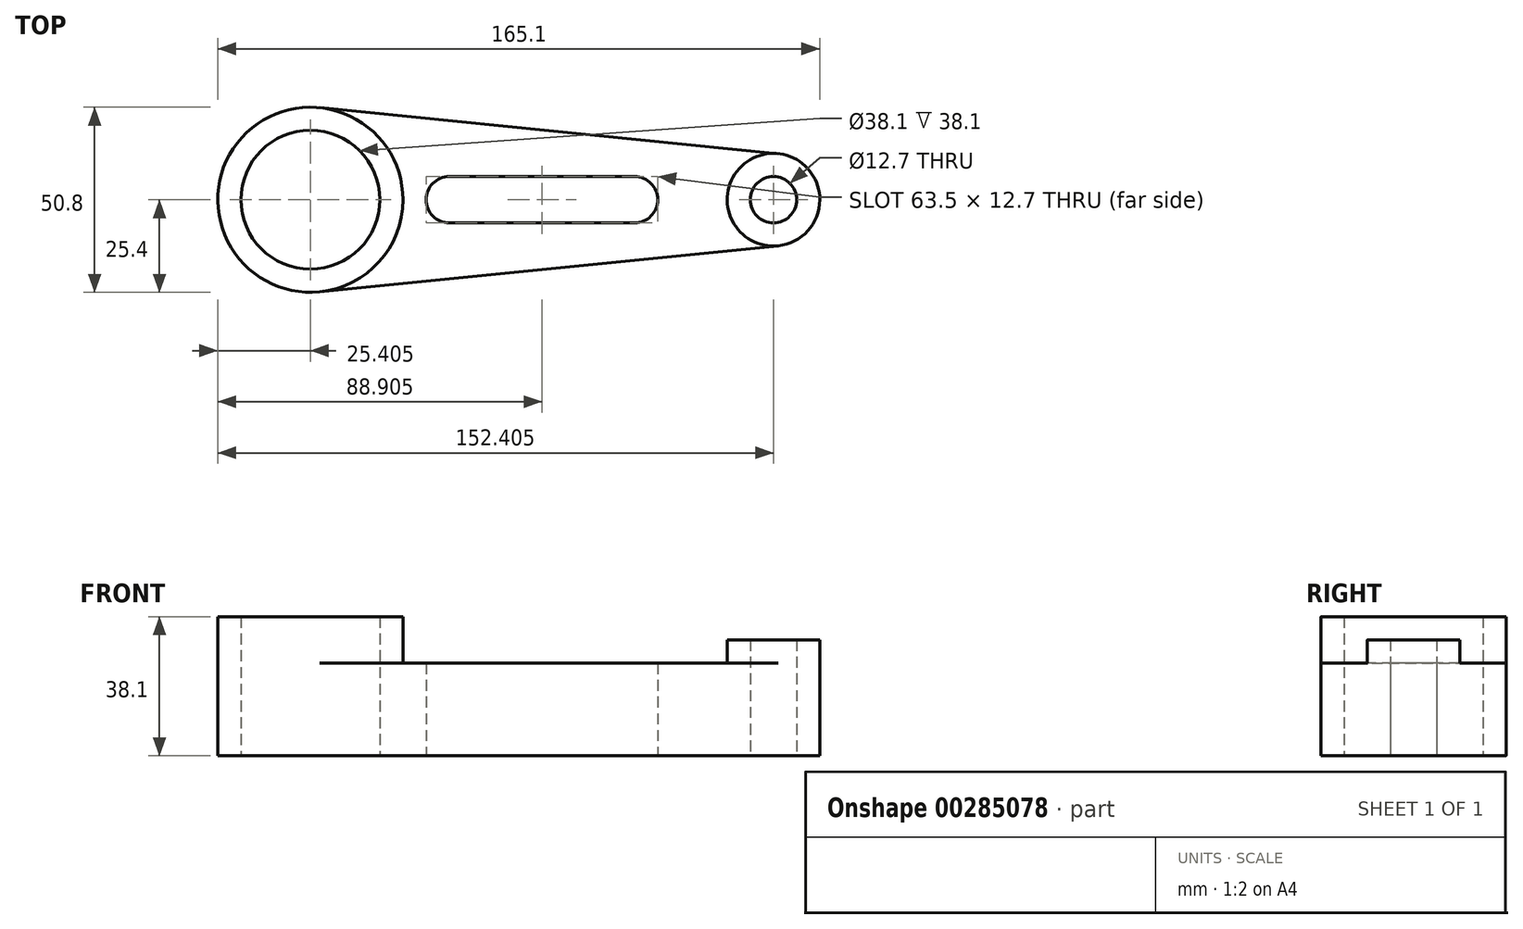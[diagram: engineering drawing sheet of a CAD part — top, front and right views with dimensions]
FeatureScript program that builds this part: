
annotation { "Feature Type Name" : "Feature", "Feature Type Description" : "" }
export const myFeature = defineFeature(function(context is Context, id is Id, definition is map)
    precondition{}
    {
        {
            var Q0;
            Q0=qCreatedBy(makeId("Top.planeOp"),FACE);
            var sketch = newSketch(context, id + "F0", { "sketchPlane" : qUnion([Q0])});
            skCircle(sketch, "E0", {"center": v(-142.8, 0) * mm, "radius": 25.4 * mm});
            skCircle(sketch, "E1", {"center": v(-142.8, 0) * mm, "radius": 19.05 * mm});
            skCircle(sketch, "E2", {"center": v(-104.7, 0) * mm, "radius": 6.35 * mm});
            skCircle(sketch, "E3", {"center": v(-53.9, 0) * mm, "radius": 6.35 * mm});
            skCircle(sketch, "E4", {"center": v(-15.8, 0) * mm, "radius": 12.7 * mm});
            skCircle(sketch, "E5", {"center": v(-15.8, 0) * mm, "radius": 6.35 * mm});
            skLineSegment(sketch, "E6", {"start": v(-140.27, 25.27) * mm, "end": v(-14.54, 12.64) * mm});
            skLineSegment(sketch, "E7", {"start": v(-140.27, -25.27) * mm, "end": v(-14.54, -12.64) * mm});
            skLineSegment(sketch, "E8", {"start": v(-104.7, 6.35) * mm, "end": v(-53.9, 6.35) * mm});
            skLineSegment(sketch, "E9", {"start": v(-104.7, -6.35) * mm, "end": v(-53.9, -6.35) * mm});
            skSolve(sketch);
        }
        {
            var Q0;
            Q0=makeQuery(id+"F0.imprint","IMPRINT",FACE,{"disambiguationData":[TD([[makeQuery(id+"F0.imprint","IMPRINT",EDGE,{"derivedFrom":sQuery(id+"F0.wireOp",EDGE,"E1")}),-1.0]])]});
            extrude(context, id + "F1", {"entities" : qUnion([Q0]), "depth" : 38.1 * mm});
        }
        {
            var Q0;
            {var subQ0=sQuery(id+"F0.wireOp",EDGE,"E6");Q0=makeQuery(id+"F0.imprint","IMPRINT",FACE,{"disambiguationData":[TD([[makeQuery(id+"F0.imprint","IMPRINT",EDGE,{"derivedFrom":subQ0}),-1.0]])]});}
            extrude(context, id + "F2", {"entities" : qUnion([Q0]), "operationType" : NewBodyOperationType.ADD, "depth" : 25.4 * mm});
        }
        {
            var Q0;
            Q0=makeQuery(id+"F0.imprint","IMPRINT",FACE,{"disambiguationData":[TD([[makeQuery(id+"F0.imprint","IMPRINT",EDGE,{"derivedFrom":sQuery(id+"F0.wireOp",EDGE,"E5")}),-1.0]])]});
            extrude(context, id + "F3", {"entities" : qUnion([Q0]), "operationType" : NewBodyOperationType.ADD, "depth" : 31.75 * mm});
        }
    });
